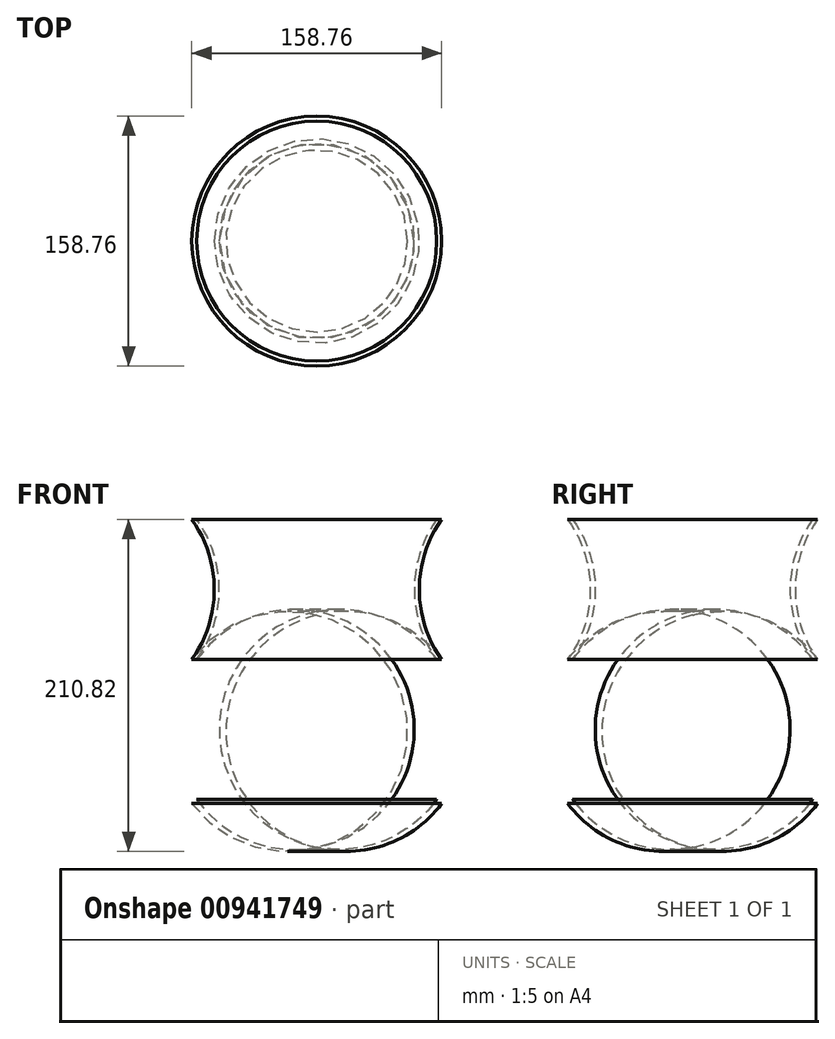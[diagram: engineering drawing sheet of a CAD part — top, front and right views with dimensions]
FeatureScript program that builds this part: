
annotation { "Feature Type Name" : "Feature", "Feature Type Description" : "" }
export const myFeature = defineFeature(function(context is Context, id is Id, definition is map)
    precondition{}
    {
        {
            var Q0;
            Q0=qCreatedBy(makeId("Front.planeOp"),FACE);
            var sketch = newSketch(context, id + "F0", { "sketchPlane" : qUnion([Q0])});
            skLineSegment(sketch, "E0", {"start": v(0, 0) * mm, "end": v(0, 76.2) * mm, "construction": true});
            skLineSegment(sketch, "E1", {"start": v(-76.2, 0) * mm, "end": v(-76.2, 88.9) * mm, "construction": true});
            skLineSegment(sketch, "E2", {"start": v(-76.2, 88.9) * mm, "end": v(-76.2, 177.8) * mm, "construction": true});
            skArc(sketch, "E3", {"start": v(-76.2, 88.9) * mm, "mid": v(-90.5, 44.45) * mm, "end": v(-76.2, 0) * mm});
            skArc(sketch, "E4", {"start": v(-76.2, 88.9) * mm, "mid": v(-61.9, 133.35) * mm, "end": v(-76.2, 177.8) * mm});
            skLineSegment(sketch, "E5", {"start": v(0, 0) * mm, "end": v(-76.2, 0) * mm});
            skLineSegment(sketch, "E6", {"start": v(0, 0) * mm, "end": v(0, -2.54) * mm});
            skLineSegment(sketch, "E7", {"start": v(0, -2.54) * mm, "end": v(-79.38, -2.54) * mm});
            skLineSegment(sketch, "E8", {"start": v(-79.38, -2.54) * mm, "end": v(-79.38, 88.9) * mm, "construction": true});
            skLineSegment(sketch, "E9", {"start": v(-79.38, 88.9) * mm, "end": v(-79.38, 177.8) * mm, "construction": true});
            skArc(sketch, "E10", {"start": v(-79.38, 88.9) * mm, "mid": v(-94.62, 43.18) * mm, "end": v(-79.38, -2.54) * mm});
            skArc(sketch, "E11", {"start": v(-79.38, 88.9) * mm, "mid": v(-65.07, 133.35) * mm, "end": v(-79.38, 177.8) * mm});
            skLineSegment(sketch, "E12", {"start": v(-79.38, 177.8) * mm, "end": v(-76.2, 177.8) * mm});
            skSolve(sketch);
        }
        {
            var Q0;
            Q0=makeQuery(id+"F0.imprint","IMPRINT",FACE,{"disambiguationData":[TD([[makeQuery(id+"F0.imprint","IMPRINT",EDGE,{"derivedFrom":sQuery(id+"F0.wireOp",EDGE,"E3")}),-1.0]])]});
            var Q1;
            Q1=sQuery(id+"F0.wireOp",EDGE,"E0");
            revolve(context, id + "F1", {"surfaceOperationType" : NewSurfaceOperationType.NEW, "entities" : qUnion([Q0]), "axis" : qUnion([Q1]), "revolveType" : RevolveType.FULL});
        }
    });
